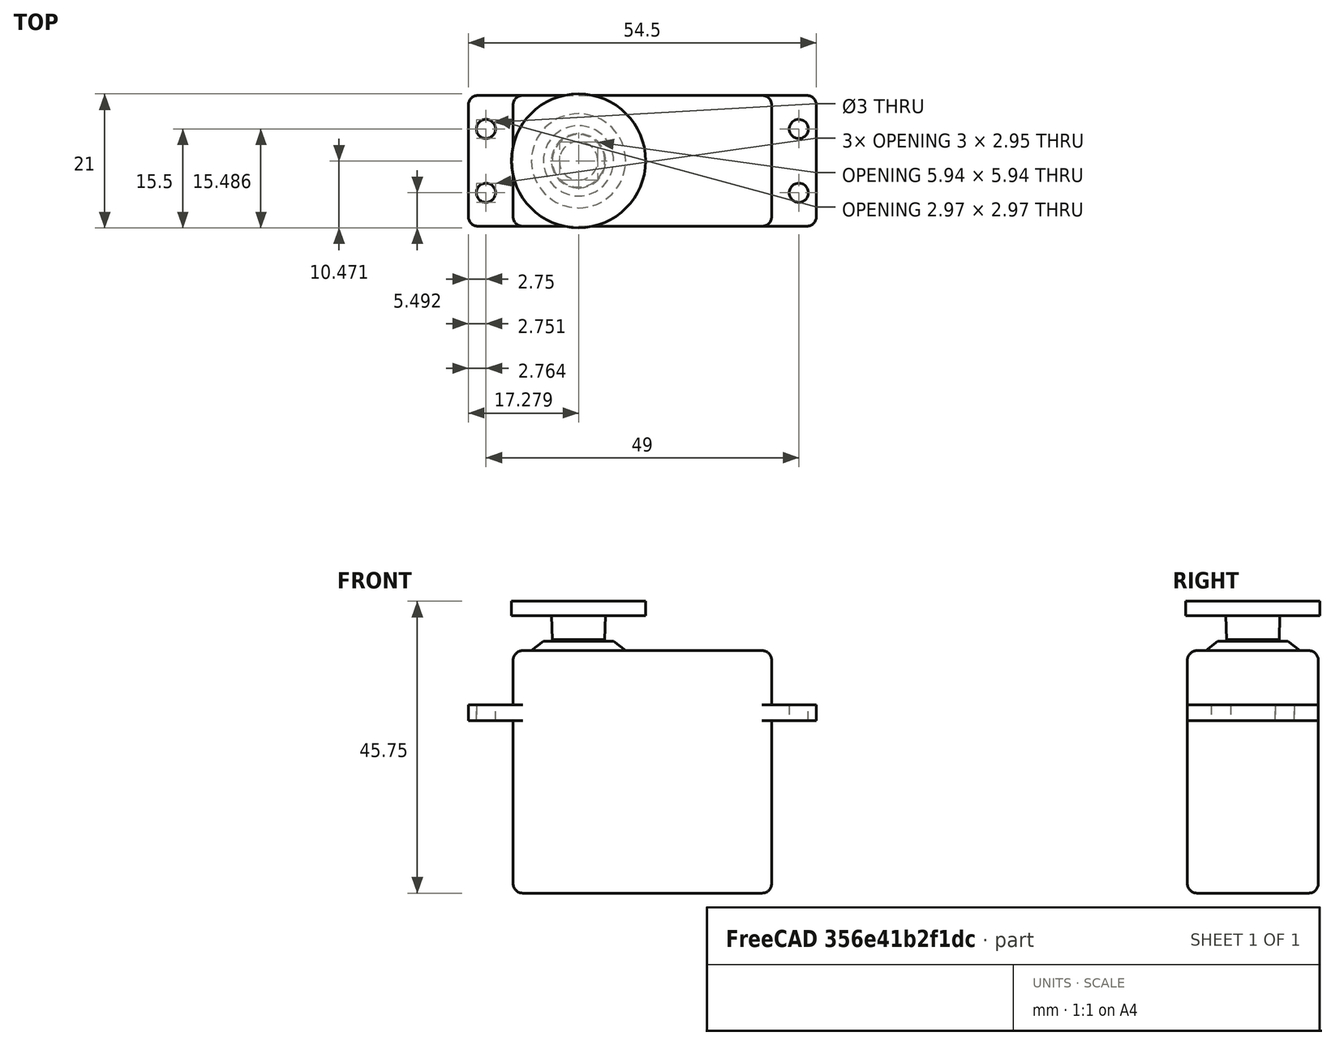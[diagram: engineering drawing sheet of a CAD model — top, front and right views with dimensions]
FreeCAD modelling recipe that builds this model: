
FCSTD DOCUMENT
Label: HD-1501MG-servo
License: CC-BY 3.0
LicenseURL: http://creativecommons.org/licenses/by/3.0/
objects: Part::Fillet×5, Part::Cut×4, Part::Cylinder×3, Part::FeaturePython×3, Part::Box×2, Part::Cone×2, Part::MultiFuse×1
note: 20 computed .brp shape members not serialized (recipe doc carries the construction recipe); baked Part::Feature solids carry a one-line shape summary decoded from their .brp

FEATURE [Part::Cylinder] Cylinder  label="ServoHorn"
  Angle = 360
  Height = 2.25
  Placement = pos=(0,0,43.5) rot=(0,0,1;0rad)
  Radius = 10.5
FEATURE [Part::Box] Box  label="ServoBody"
  Height = 38
  Length = 40.5
  Placement = pos=(-10.25,-10.25,0) rot=(0,0,1;0rad)
  Width = 20.5
FEATURE [Part::Box] Box001  label="servo_lugs"
  Height = 2.5
  Length = 54.5
  Placement = pos=(-17.25,-10.25,27) rot=(0,0,1;0rad)
  Width = 20.5
FEATURE [Part::Cone] Cone  label="ServoBodyCone"
  Angle = 360
  Height = 2
  Placement = pos=(0,0,37.5) rot=(0,0,1;0rad)
  Radius1 = 8
  Radius2 = 5.5
FEATURE [Part::Cone] Cone001
  Angle = 360
  Height = 4
  Placement = pos=(0,0,39.75) rot=(0,0,1;0rad)
  Radius1 = 4.12
  Radius2 = 4.25
FEATURE [Part::Cylinder] Cylinder001  label="shaft"
  Angle = 360
  Height = 4.5
  Placement = pos=(0,0,38.5) rot=(0,0,1;0rad)
  Radius = 3
FEATURE [Part::Cylinder] Cylinder002  label="Screw_hole1"
  Angle = 360
  Height = 5
  Placement = pos=(-14.5,5,26) rot=(0,0,1;0rad)
  Radius = 1.5
FEATURE [Part::FeaturePython] Clone  label="Screw_hole2"  # Draft clone (typed FeaturePython)
  Objects = -> [Cylinder002]
  Placement = pos=(-14.5,-5,26) rot=(0,0,1;0rad)
  Scale = (1,1,1)
FEATURE [Part::FeaturePython] Clone001  label="Screw_hole3"  # Draft clone (typed FeaturePython)
  Objects = -> [Cylinder002]
  Placement = pos=(34.5,5,26) rot=(0,0,1;0rad)
  Scale = (1,1,1)
FEATURE [Part::FeaturePython] Clone002  label="Screw_hole4"  # Draft clone (typed FeaturePython)
  Objects = -> [Clone001]
  Placement = pos=(34.5,-5,26) rot=(0,0,1;0rad)
  Scale = (1,1,1)
FEATURE [Part::Cut] Cut
  Base = -> Box001
  Tool = -> Cylinder002
FEATURE [Part::Cut] Cut001
  Base = -> Cut
  Tool = -> Clone
FEATURE [Part::Cut] Cut002
  Base = -> Cut001
  Tool = -> Clone001
FEATURE [Part::Cut] Cut003  label="ServoLugs"
  Base = -> Cut002
  Tool = -> Clone002
FEATURE [Part::Fillet] Fillet
  Base = -> Cut003
  Edges = 1 edges r=1.5: [Edge6]
FEATURE [Part::Fillet] Fillet001
  Base = -> Fillet
  Edges = 1 edges r=1.5: [Edge31]
FEATURE [Part::Fillet] Fillet002
  Base = -> Fillet001
  Edges = 1 edges r=1.5: [Edge24]
FEATURE [Part::Fillet] Fillet003  label="servo_lugs001"
  Base = -> Fillet002
  Edges = 1 edges r=1.5: [Edge24]
FEATURE [Part::Fillet] Fillet004  label="ServoBody001"
  Base = -> Box
  Edges = 12 edges r=1.5: [Edge1,Edge2,Edge3,Edge4,Edge5,Edge6,Edge7,Edge8,Edge9,Edge10,Edge11,Edge12]
FEATURE [Part::MultiFuse] Fusion  label="Servo"
  Shapes = -> [Cylinder,Cone,Cone001,Cylinder001,Fillet003,Fillet004]
